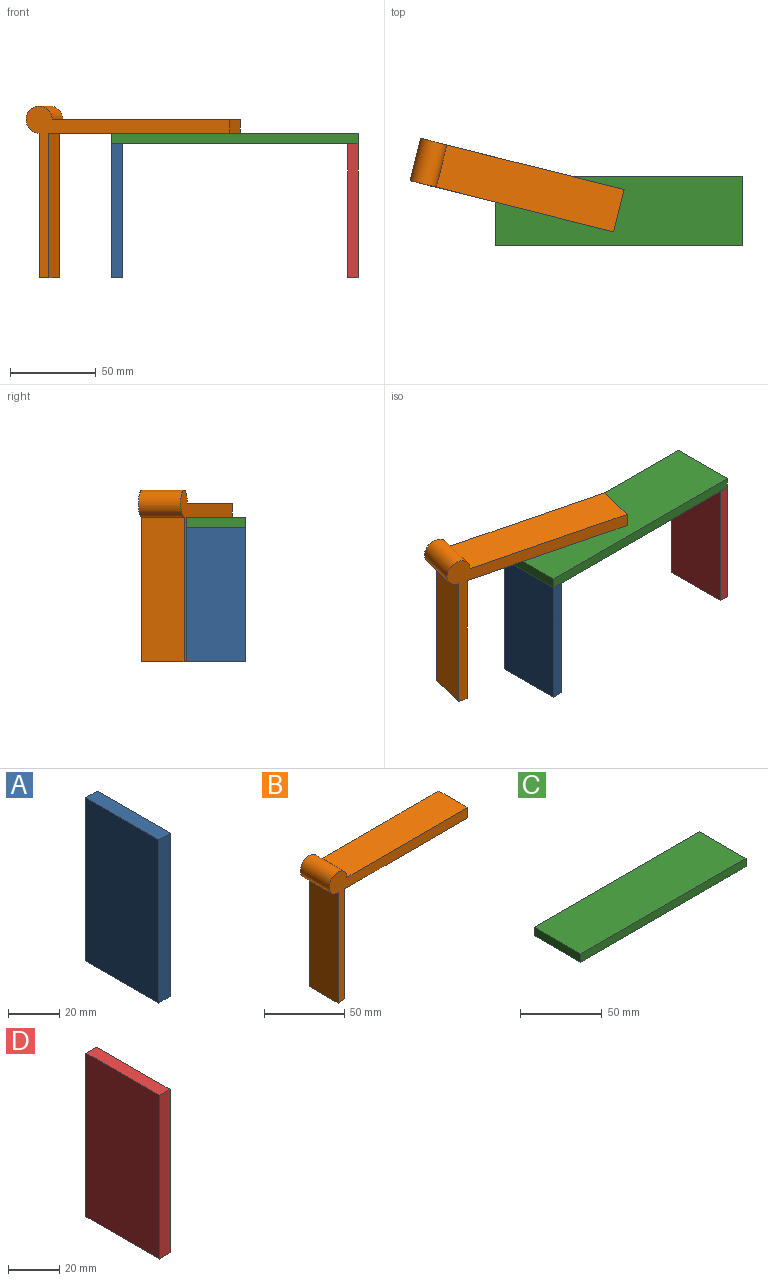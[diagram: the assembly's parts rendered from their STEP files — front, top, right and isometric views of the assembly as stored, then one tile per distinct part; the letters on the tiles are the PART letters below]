
ASSEMBLY  parts=4 mates=5
PART A: 6 faces, bbox 6.4x40.4x78.1 mm
  f0: plane 78.09x6.42mm, normal (0,-1,0), area 501mm2, adj f1,f3,f4,f5
  f1: plane 78.09x40.39mm, normal (-1,0,0), area 3153.6mm2, adj f0,f2,f3,f4
  f2: plane 78.09x6.42mm, normal (0,1,0), area 501mm2, adj f1,f3,f4,f5
  f3: plane 40.39x6.42mm, normal (0,0,-1), area 259.1mm2, adj f0,f1,f2,f5
  f4: plane 40.39x6.42mm, normal (0,0,1), area 259.1mm2, adj f0,f1,f2,f5
  f5: plane 78.09x40.39mm, normal (1,0,0), area 3153.6mm2, adj f0,f2,f3,f4
PART B: 9 faces, bbox 122.3x25.4x100.1 mm
  f0: plane 106.53x25.4mm, normal (0,0,1), area 2705.8mm2, adj f1,f6,f7,f8
  f1: cylinder r=7.88mm len=25.4mm, axis (0,1,0), area 943.4mm2, adj f0,f2,f7,f8
  f2: plane 84.29x25.4mm, normal (-1,0,0), area 2140.9mm2, adj f1,f3,f7,f8
  f3: plane 25.4x5.86mm, normal (0.03,0,-1), area 149mm2, adj f2,f4,f7,f8
  f4: plane 84.13x25.4mm, normal (1,0,0), area 2137mm2, adj f3,f5,f7,f8
  f5: plane 108.55x25.4mm, normal (0,0,-1), area 2757.1mm2, adj f4,f6,f7,f8
  f6: plane 25.4x7.88mm, normal (1,0,0), area 200.2mm2, adj f0,f5,f7,f8
  f7: plane 122.29x100.05mm, normal (0,-1,0), area 1541.9mm2, adj f0,f1,f2,f3,f4,f5,f6
  f8: plane 122.29x100.05mm, normal (0,1,0), area 1541.9mm2, adj f0,f1,f2,f3,f4,f5,f6
PART C: 6 faces, bbox 143.5x40.4x6.2 mm
  f0: plane 143.52x40.39mm, normal (0,0,-1), area 5796.3mm2, adj f1,f3,f4,f5
  f1: plane 40.39x6.23mm, normal (1,0,0), area 251.7mm2, adj f0,f2,f4,f5
  f2: plane 143.52x40.39mm, normal (0,0,1), area 5796.3mm2, adj f1,f3,f4,f5
  f3: plane 40.39x6.23mm, normal (-1,0,0), area 251.7mm2, adj f0,f2,f4,f5
  f4: plane 143.52x6.23mm, normal (0,-1,0), area 894.5mm2, adj f0,f1,f2,f3
  f5: plane 143.52x6.23mm, normal (0,1,0), area 894.5mm2, adj f0,f1,f2,f3
PART D: 6 faces, bbox 5.9x40.4x77.9 mm
  f0: plane 77.9x5.87mm, normal (0,-1,0), area 456.9mm2, adj f1,f3,f4,f5
  f1: plane 40.39x5.87mm, normal (0,0,1), area 236.9mm2, adj f0,f2,f3,f4
  f2: plane 77.9x5.87mm, normal (0,1,0), area 456.9mm2, adj f1,f3,f4,f5
  f3: plane 77.9x40.39mm, normal (-1,0,0), area 3146.2mm2, adj f0,f1,f2,f5
  f4: plane 77.9x40.39mm, normal (1,0,0), area 3146.2mm2, adj f0,f1,f2,f5
  f5: plane 40.39x5.87mm, normal (0,0,-1), area 236.9mm2, adj f0,f2,f3,f4
PLACE A t=(-17.69,-7.19,-3.76)mm
PLACE B rot(axis=(0,0,-1),14.2deg) t=(-71.91,-0.91,2.65)mm
PLACE C t=(-17.69,-7.19,-3.76)mm
PLACE D t=(-17.69,-7.19,-3.76)mm fixed
MATE fastened C.f0 <-> D.f1  axis (0,0,1) through (52.88,-7.19,12.92)mm
MATE cylindrical B.f0 <-> C.f2  axis (0,0,1) through (-18.89,-27.39,27.03)mm
MATE planar C.f0 <-> A.f4  axis (0,0,-1) through (-18.89,-27.39,12.92)mm
MATE planar C.f2 <-> B.f5  axis (0,0,1) through (-18.89,-27.39,19.15)mm
MATE fastened C.f0 <-> A.f4  axis (0,0,1) through (-90.65,-47.58,12.92)mm
